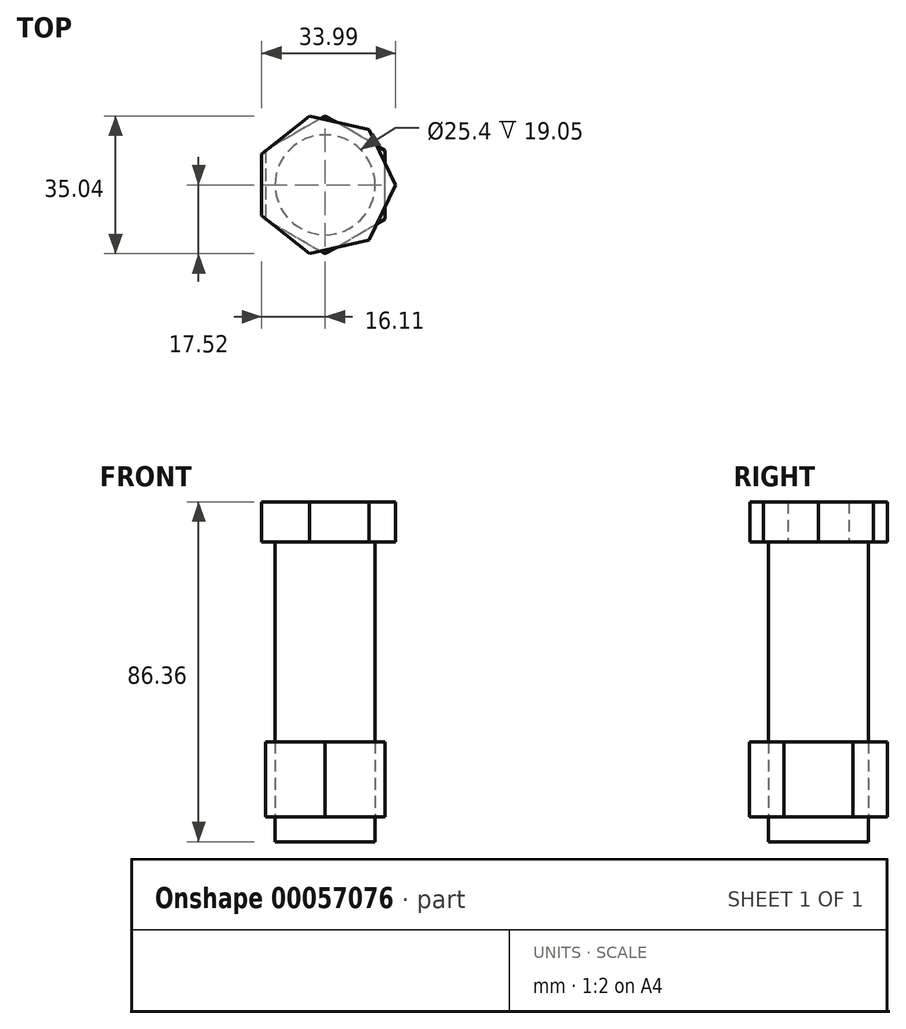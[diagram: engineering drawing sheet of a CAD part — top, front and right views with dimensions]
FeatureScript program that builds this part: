
annotation { "Feature Type Name" : "Feature", "Feature Type Description" : "" }
export const myFeature = defineFeature(function(context is Context, id is Id, definition is map)
    precondition{}
    {
        {
            var Q0;
            Q0=qCreatedBy(makeId("Top.planeOp"),FACE);
            var sketch = newSketch(context, id + "F0", { "sketchPlane" : qUnion([Q0])});
            skCircle(sketch, "E0", {"center": v(0, 0) * mm, "radius": 12.7 * mm});
            skSolve(sketch);
        }
        {
            var Q0;
            Q0 = qSketchRegion(id + "F0", true);
            extrude(context, id + "F1", {"entities" : qUnion([Q0]), "depth" : 76.2 * mm});
        }
        {
            var Q0;
            Q0=makeQuery(id+"F1.opExtrude","CAP_FACE",FACE,{"disambiguationData":[OSD([sQuery(id+"F0.wireOp",EDGE,"E0")])],"isStart":false});
            var sketch = newSketch(context, id + "F2", { "sketchPlane" : qUnion([Q0])});
            skCircle(sketch, "E1.cCircle", {"center": v(0, 0) * mm, "radius": 16.11 * mm, "construction": true});
            skLineSegment(sketch, "E1.0", {"start": v(-16.11, -7.76) * mm, "end": v(-16.11, 7.76) * mm});
            skLineSegment(sketch, "E1.1", {"start": v(-16.11, 7.76) * mm, "end": v(-3.98, 17.44) * mm});
            skLineSegment(sketch, "E1.2", {"start": v(-3.98, 17.44) * mm, "end": v(11.15, 13.98) * mm});
            skLineSegment(sketch, "E1.3", {"start": v(11.15, 13.98) * mm, "end": v(17.88, 0) * mm});
            skLineSegment(sketch, "E1.4", {"start": v(17.88, 0) * mm, "end": v(11.15, -13.98) * mm});
            skLineSegment(sketch, "E1.5", {"start": v(11.15, -13.98) * mm, "end": v(-3.98, -17.44) * mm});
            skLineSegment(sketch, "E1.6", {"start": v(-3.98, -17.44) * mm, "end": v(-16.11, -7.76) * mm});
            skPoint(sketch, "E1.0.midPoint", {"position": v(-16.11, 0) * mm});
            skSolve(sketch);
        }
        {
            var Q0;
            Q0=makeQuery(id+"F2.imprint","IMPRINT",FACE,{"disambiguationData":[TD([[makeQuery(id+"F2.imprint","IMPRINT",EDGE,{"derivedFrom":sQuery(id+"F2.wireOp",EDGE,"E1.0")}),-1.0]])]});
            var Q1;
            Q1=makeQuery(id+"F2.imprint","IMPRINT",FACE,{"disambiguationData":[TD([[makeQuery(id+"F2.imprint","IMPRINT",EDGE,{"derivedFrom":makeQuery(id+"F1.opExtrude","CAP_EDGE",EDGE,{"disambiguationData":[OSD([sQuery(id+"F0.wireOp",EDGE,"E0")])],"isStart":false})}),1.0]])]});
            extrude(context, id + "F3", {"entities" : qUnion([Q0, Q1]), "operationType" : NewBodyOperationType.ADD, "depth" : 10.16 * mm});
        }
        {
            var Q0;
            Q0=makeQuery(id+"F1.opExtrude","CAP_FACE",FACE,{"disambiguationData":[OSD([sQuery(id+"F0.wireOp",EDGE,"E0")])],"isStart":true});
            var sketch = newSketch(context, id + "F4", { "sketchPlane" : qUnion([Q0])});
            skCircle(sketch, "E2.cCircle", {"center": v(0, 0) * mm, "radius": 15.17 * mm, "construction": true});
            skLineSegment(sketch, "E2.0", {"start": v(-15.17, -8.76) * mm, "end": v(-15.17, 8.76) * mm});
            skLineSegment(sketch, "E2.1", {"start": v(-15.17, 8.76) * mm, "end": v(0, 17.52) * mm});
            skLineSegment(sketch, "E2.2", {"start": v(0, 17.52) * mm, "end": v(15.17, 8.76) * mm});
            skLineSegment(sketch, "E2.3", {"start": v(15.17, 8.76) * mm, "end": v(15.17, -8.76) * mm});
            skLineSegment(sketch, "E2.4", {"start": v(15.17, -8.76) * mm, "end": v(0, -17.52) * mm});
            skLineSegment(sketch, "E2.5", {"start": v(0, -17.52) * mm, "end": v(-15.17, -8.76) * mm});
            skPoint(sketch, "E2.0.midPoint", {"position": v(-15.17, 0) * mm});
            skCircle(sketch, "E3", {"center": v(0, 0) * mm, "radius": 12.7 * mm});
            skSolve(sketch);
        }
        {
            var Q0;
            Q0=makeQuery(id+"F4.imprint","IMPRINT",FACE,{"disambiguationData":[TD([[makeQuery(id+"F4.imprint","IMPRINT",EDGE,{"derivedFrom":sQuery(id+"F4.wireOp",EDGE,"E2.0")}),-1.0]])]});
            extrude(context, id + "F5", {"entities" : qUnion([Q0]), "oppositeDirection" : true, "depth" : 25.4 * mm});
        }
        {
            var Q0;
            Q0=makeQuery(id+"F5.opExtrude","CAP_FACE",FACE,{"disambiguationData":[OSD([sQuery(id+"F4.wireOp",EDGE,"E2.0"),sQuery(id+"F4.wireOp",EDGE,"E2.1"),sQuery(id+"F4.wireOp",EDGE,"E2.2"),sQuery(id+"F4.wireOp",EDGE,"E2.3"),sQuery(id+"F4.wireOp",EDGE,"E2.4"),sQuery(id+"F4.wireOp",EDGE,"E2.5"),sQuery(id+"F4.wireOp",EDGE,"E3")])],"isStart":true});
            extrude(context, id + "F6", {"entities" : qUnion([Q0]), "operationType" : NewBodyOperationType.REMOVE, "oppositeDirection" : true, "depth" : 6.35 * mm});
        }
    });
